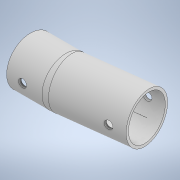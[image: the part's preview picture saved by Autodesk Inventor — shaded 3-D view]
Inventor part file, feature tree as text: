
AUTODESK INVENTOR PART (.ipt)
format: ipt  version: 2022 (Build 260153000, 153)  size: 242,176 bytes
history: native  units: mm
features: sketch x4, extrude x2, sweep x1
ambient origin geometry x8: Origin, YZ Plane, XZ Plane, XY Plane, X Axis, Y Axis, Z Axis, Center Point
bodies: Body1 (feature_tree)
feature tree (7):
  sweep  "Sweep1"
  extrude  "Extrusion8"  Depth=30.194196mm
  extrude  "Extrusion9"  Depth=10.0mm
  sketch  "Sketch5"  dims[d31=34.456mm d122=14.0mm]
  sketch  "Sketch6"  dims[d123=27.0mm d124=30.194196mm]
  sketch  "Sketch7"  dims[d125=10.0mm d126=16.0mm]
  sketch  "Sketch8"  dims[d127=18.0mm d128=0.0mm d129=0.0mm d130=6.0mm d131=3.0mm d132=25.0mm d133=0.0mm d134=6.0mm d135=3.0mm d136=25.0mm d137=0.0mm d138=0.01mm d139=0.01mm]
